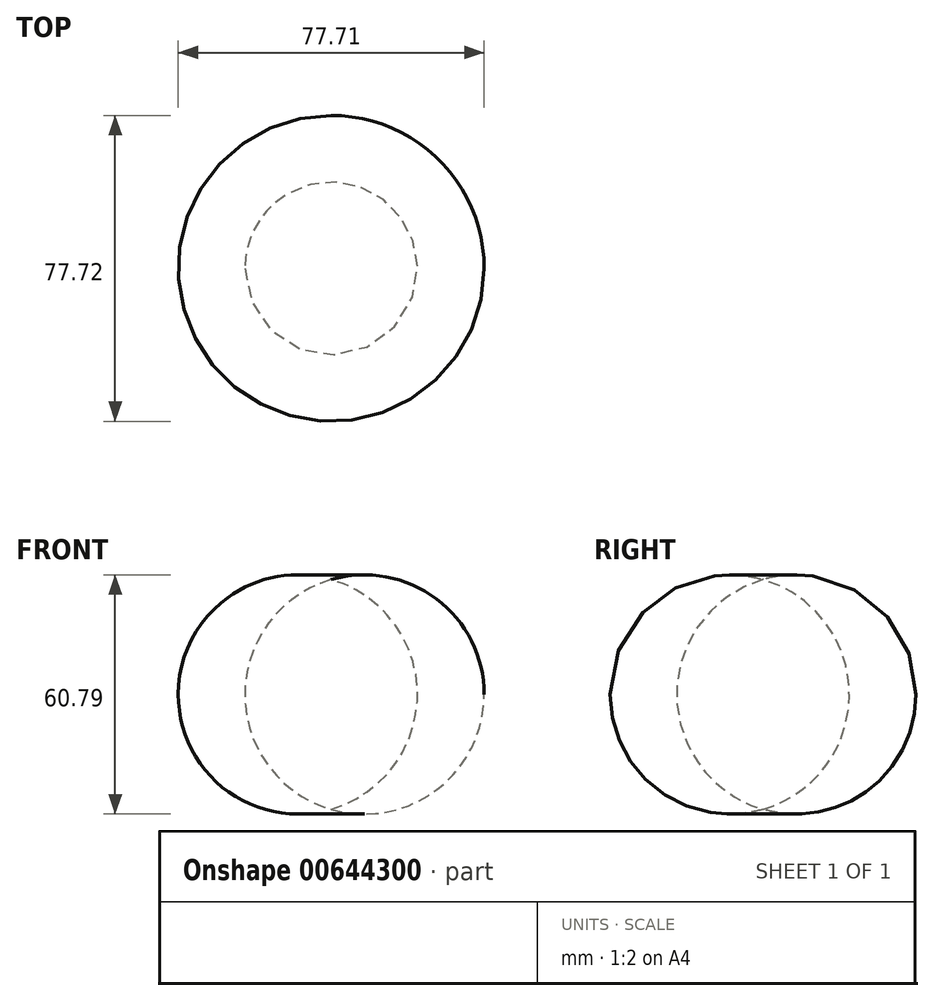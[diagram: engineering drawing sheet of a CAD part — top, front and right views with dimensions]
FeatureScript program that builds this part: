
annotation { "Feature Type Name" : "Feature", "Feature Type Description" : "" }
export const myFeature = defineFeature(function(context is Context, id is Id, definition is map)
    precondition{}
    {
        {
            var Q0;
            Q0=qCreatedBy(makeId("Front.planeOp"),FACE);
            var sketch = newSketch(context, id + "F0", { "sketchPlane" : qUnion([Q0])});
            skArc(sketch, "E0", {"start": v(-5.7, 45.26) * mm, "mid": v(-44.58, 16.1) * mm, "end": v(-5.74, -13.1) * mm});
            skLineSegment(sketch, "E1", {"start": v(-5.7, 45.26) * mm, "end": v(-5.74, -13.1) * mm});
            skSolve(sketch);
        }
        {
            var Q0;
            Q0=makeQuery(id+"F0.imprint","IMPRINT",FACE,{"disambiguationData":[TD([[makeQuery(id+"F0.imprint","IMPRINT",EDGE,{"derivedFrom":sQuery(id+"F0.wireOp",EDGE,"E0")}),1.0]])]});
            var Q1;
            Q1=sQuery(id+"F0.wireOp",EDGE,"E1");
            revolve(context, id + "F1", {"entities" : qUnion([Q0]), "axis" : qUnion([Q1]), "revolveType" : RevolveType.FULL});
        }
    });
